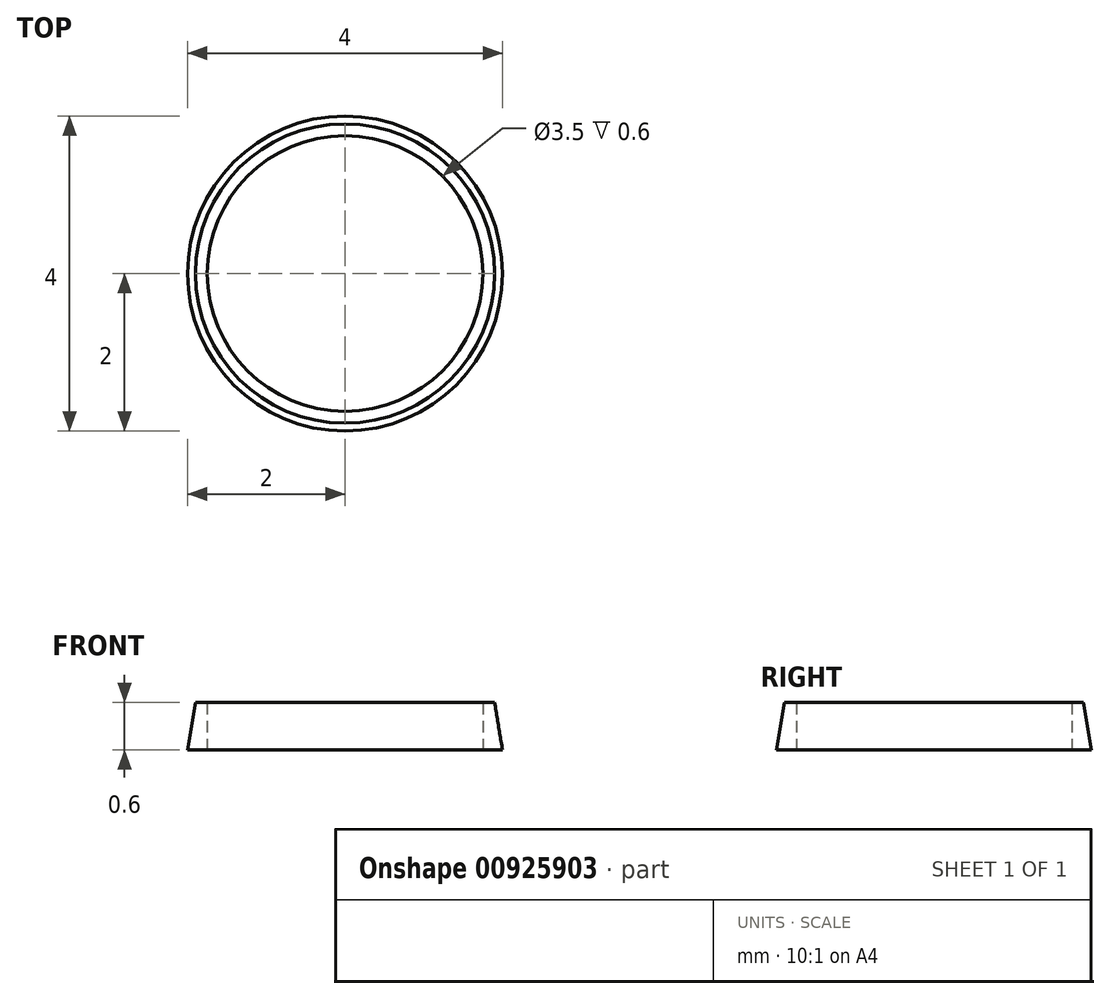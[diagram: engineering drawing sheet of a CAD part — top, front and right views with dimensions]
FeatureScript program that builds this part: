
annotation { "Feature Type Name" : "Feature", "Feature Type Description" : "" }
export const myFeature = defineFeature(function(context is Context, id is Id, definition is map)
    precondition{}
    {
        {
            var Q0;
            Q0=qCreatedBy(makeId("Top.planeOp"),FACE);
            var sketch = newSketch(context, id + "F0", { "sketchPlane" : qUnion([Q0])});
            skCircle(sketch, "E0", {"center": v(0, 0) * mm, "radius": 2 * mm});
            skSolve(sketch);
        }
        {
            var Q0;
            Q0=qSketchRegion(id+"F0",true);
            extrude(context, id + "F1", {"entities" : qUnion([Q0]), "depth" : 0.6 * mm, "offsetDistance" : 25 * mm});
        }
        {
            var Q0;
            Q0=sQuery(id+"F0.wireOp",VERTEX,"E0.center");
            var Q1;
            Q1=makeQuery(id+"F1.opExtrude","SWEPT_BODY",BODY,{"disambiguationData":[OSD([sQuery(id+"F0.wireOp",EDGE,"E0")])]});
            hole(context, id + "F2", {"style" : HoleStyle.SIMPLE, "endStyle" : HoleEndStyle.THROUGH, "oppositeDirection" : true, "standardTappedOrClearance" : lookupTablePath({ "standard" : "ISO", "engagement" : "75%", "pitch" : "0.5 mm", "size" : "M4", "type" : "Tapped" }), "standardBlindInLast" : lookupTablePath({ "standard" : "ISO", "fit" : "Normal", "engagement" : "75%", "pitch" : "0.5 mm", "size" : "M4", "type" : "Clearance & tapped" }), "holeDiameter" : 3.5 * mm, "majorDiameter" : 4 * mm, "showTappedDepth" : true, "isTappedThrough" : true, "tappedDepth" : 1.2 * mm, "tapClearance" : 3, "startFromSketch" : true, "locations" : qUnion([Q0]), "scope" : qUnion([Q1])});
        }
        {
            var Q0;
            Q0=makeQuery(id+"F1.opExtrude","CAP_EDGE",EDGE,{"disambiguationData":[OSD([sQuery(id+"F0.wireOp",EDGE,"E0")])],"isStart":false});
            chamfer(context, id + "F3", {"entities" : qUnion([Q0]), "chamferType" : ChamferType.TWO_OFFSETS, "width1" : 0.1 * mm, "oppositeDirection" : false, "width2" : 0.6 * mm, "tangentPropagation" : true});
        }
    });
